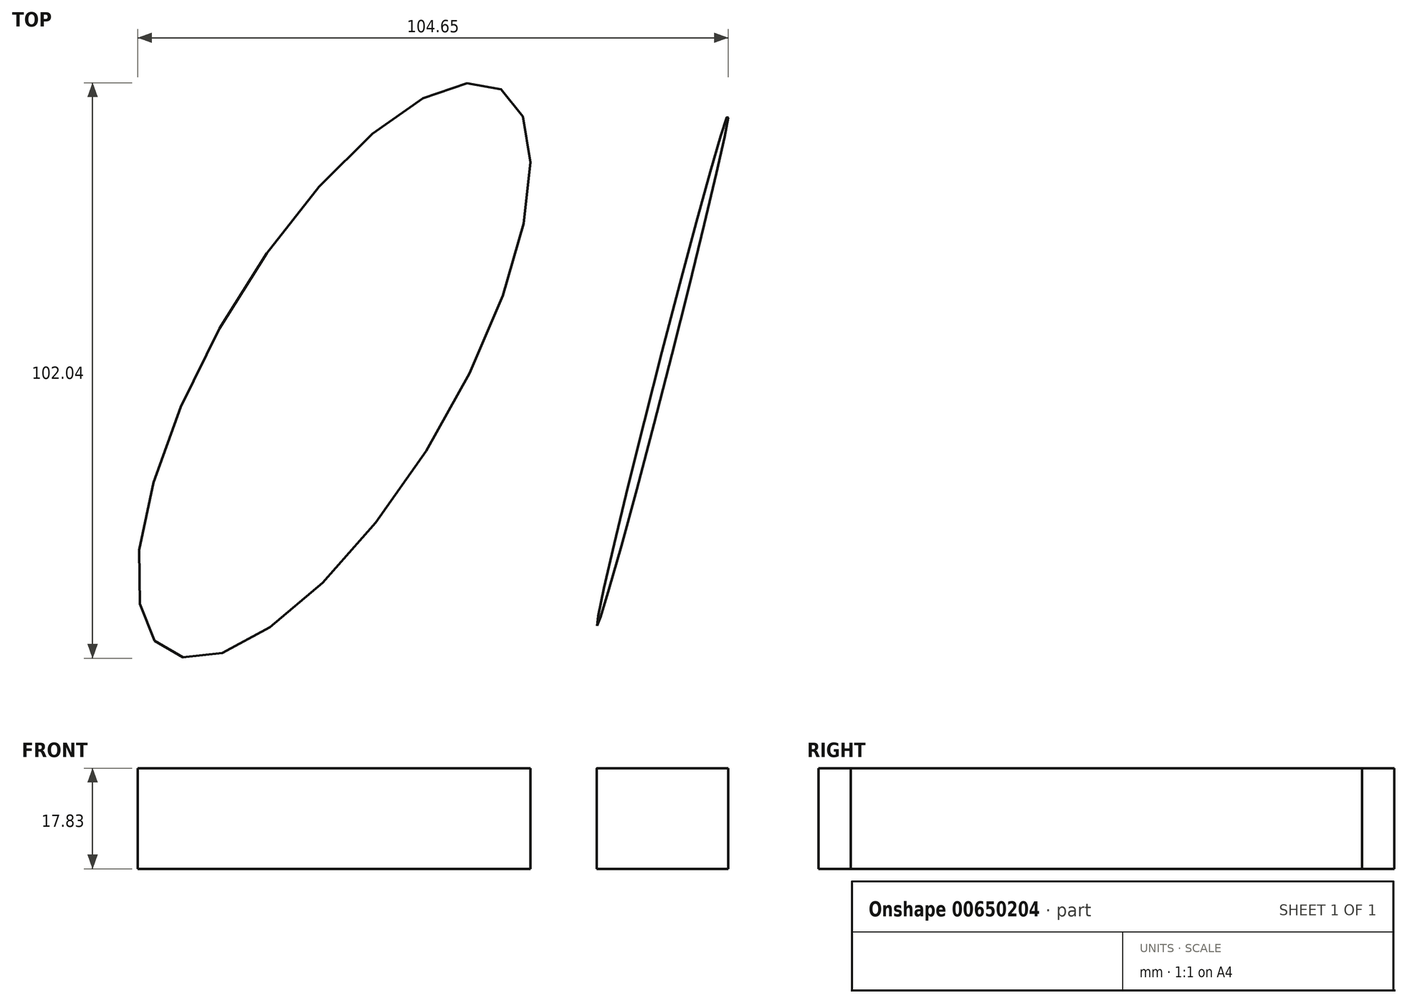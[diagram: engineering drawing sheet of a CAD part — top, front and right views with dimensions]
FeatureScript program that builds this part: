
annotation { "Feature Type Name" : "Feature", "Feature Type Description" : "" }
export const myFeature = defineFeature(function(context is Context, id is Id, definition is map)
    precondition{}
    {
        {
            var Q0;
            Q0=qCreatedBy(makeId("Top.planeOp"),FACE);
            var sketch = newSketch(context, id + "F0", { "sketchPlane" : qUnion([Q0])});
            skEllipse(sketch, "E0", {"center": v(-39.82, 0) * mm, "majorRadius": 57.96 * mm, "minorRadius": 21.34 * mm, "majorAxis": v(0.51, 0.86)});
            skEllipse(sketch, "E1", {"center": v(18.37, 0) * mm, "majorRadius": 46.75 * mm, "minorRadius": 0.91 * mm, "majorAxis": v(-0.25, -0.97)});
            skSolve(sketch);
        }
        {
            var Q0;
            Q0=makeQuery(id+"F0.imprint","IMPRINT",FACE,{"disambiguationData":[TD([[makeQuery(id+"F0.imprint","IMPRINT",EDGE,{"derivedFrom":sQuery(id+"F0.wireOp",EDGE,"E0")}),1.0]])]});
            var Q1;
            Q1=makeQuery(id+"F0.imprint","IMPRINT",FACE,{"disambiguationData":[TD([[makeQuery(id+"F0.imprint","IMPRINT",EDGE,{"derivedFrom":sQuery(id+"F0.wireOp",EDGE,"E1")}),1.0]])]});
            extrude(context, id + "F1", {"entities" : qUnion([Q0, Q1]), "depth" : 17.83 * mm, "offsetDistance" : 25.4 * mm});
        }
    });
